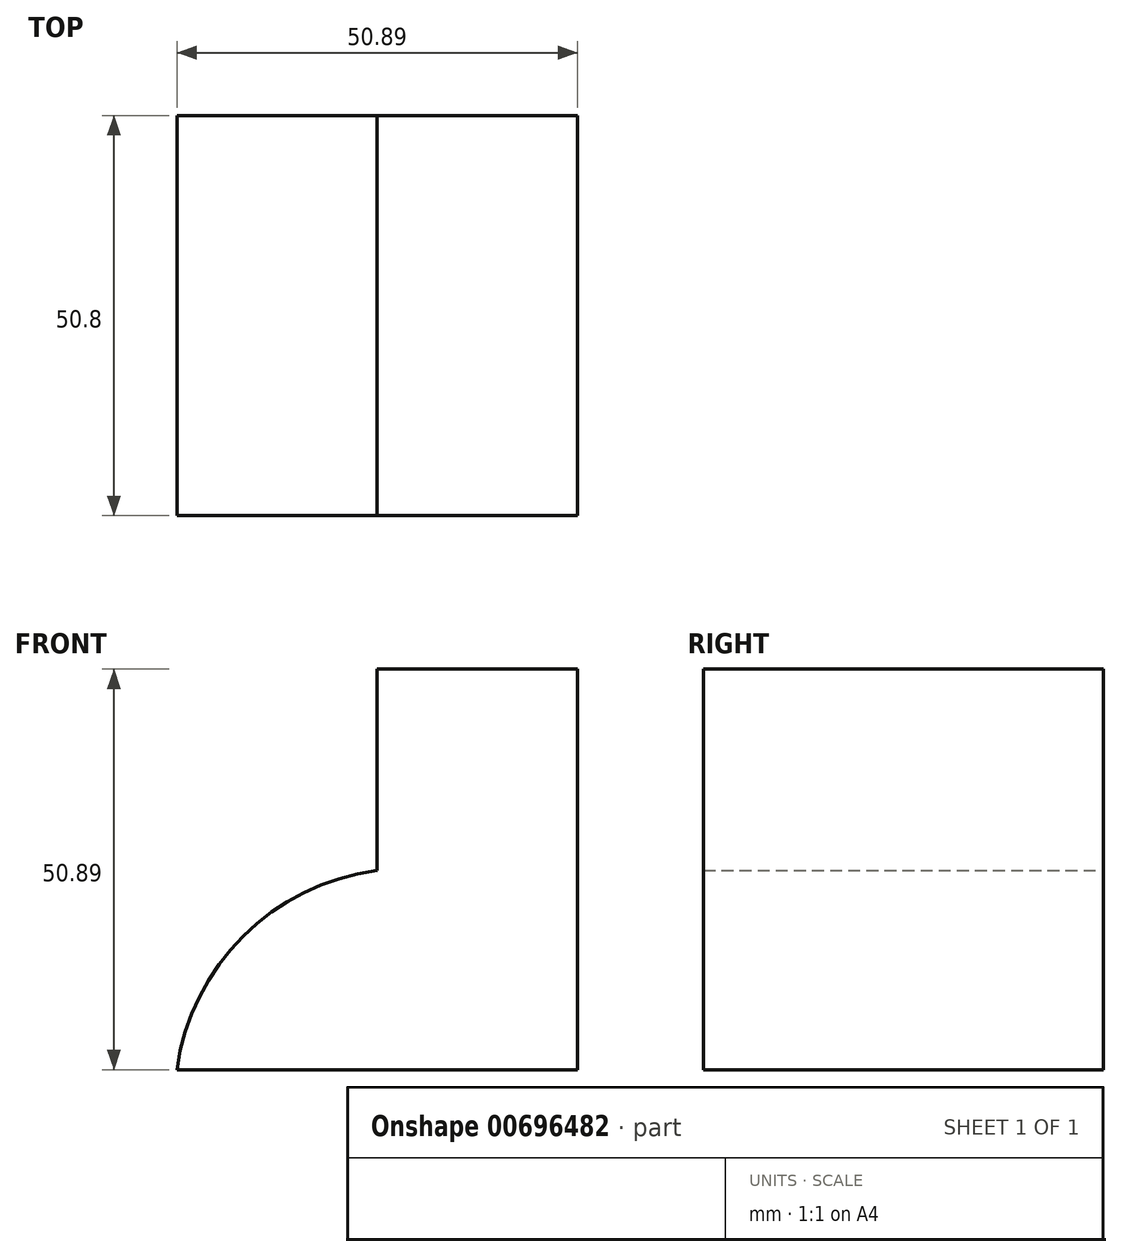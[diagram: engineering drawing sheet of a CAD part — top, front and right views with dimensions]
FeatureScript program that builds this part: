
annotation { "Feature Type Name" : "Feature", "Feature Type Description" : "" }
export const myFeature = defineFeature(function(context is Context, id is Id, definition is map)
    precondition{}
    {
        {
            var Q0;
            Q0=qCreatedBy(makeId("Front.planeOp"),FACE);
            var sketch = newSketch(context, id + "F0", { "sketchPlane" : qUnion([Q0])});
            skLineSegment(sketch, "E0", {"start": v(0, 0) * mm, "end": v(0, 50.89) * mm});
            skLineSegment(sketch, "E1", {"start": v(0, 50.89) * mm, "end": v(-25.5, 50.89) * mm});
            skLineSegment(sketch, "E2", {"start": v(-25.5, 50.89) * mm, "end": v(-25.5, 25.3) * mm});
            skLineSegment(sketch, "E3", {"start": v(0, 0) * mm, "end": v(-50.89, 0) * mm});
            skArc(sketch, "E4", {"start": v(-25.5, 25.3) * mm, "mid": v(-42.47, 16.95) * mm, "end": v(-50.89, 0) * mm});
            skSolve(sketch);
        }
        {
            var Q0;
            Q0 = qSketchRegion(id + "F0", true);
            extrude(context, id + "F1", {"entities" : qUnion([Q0]), "depth" : 50.8 * mm, "offsetDistance" : 25.4 * mm});
        }
    });
